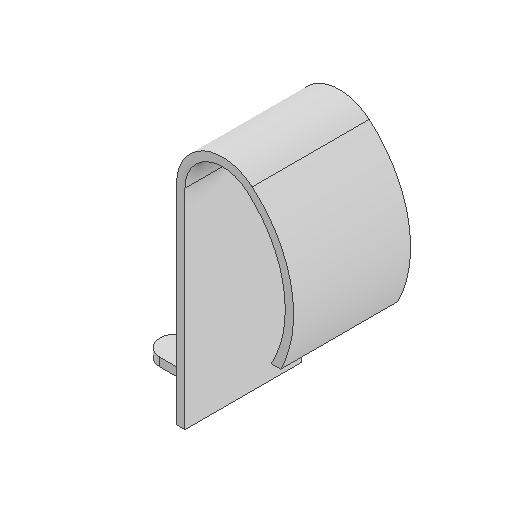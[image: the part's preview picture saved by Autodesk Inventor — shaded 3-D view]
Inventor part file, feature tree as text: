
AUTODESK INVENTOR PART (.ipt)
format: ipt  version: 2025.2 (Build 292293000, 293)  size: 118,272 bytes
history: native  units: mm
features: extrude x2, sketch x2, fillet x1
ambient origin geometry x8: Origin, YZ Plane, XZ Plane, XY Plane, X Axis, Y Axis, Z Axis, Center Point
bodies: Solid1 (feature_tree)
feature tree (5):
  extrude  "Extrusion1"  Depth=0.5mm
  extrude  "Extrusion2"  Depth=7.0mm
  fillet  "Fillet1"  Radius=7.0mm
  sketch  "Sketch1"  dims[d0=0.5mm d1=15.0mm]
  sketch  "Sketch2"  dims[d2=6.0mm d4=7.0mm d5=7.0mm d6=0.0mm d8=2.0mm d9=4.5mm d10=0.0mm d11=1.0mm]
